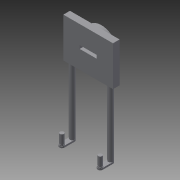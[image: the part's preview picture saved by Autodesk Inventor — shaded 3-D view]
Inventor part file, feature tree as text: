
AUTODESK INVENTOR PART (.ipt)
format: ipt  version: 2015 SP2 (Build 190223200, 223)  size: 163,328 bytes
history: native  units: mm
features: sketch x11, extrude x9
ambient origin geometry x8: Origin, YZ Plane, XZ Plane, XY Plane, X Axis, Y Axis, Z Axis, Center Point
bodies: Solid1 (feature_tree)
feature tree (20):
  sketch  "Sketch1"  dims[d0=5.1mm d1=1.0mm]
  sketch  "Sketch2"  dims[d2=15.0mm d3=12.0mm]
  extrude  "Extrusion1"  Depth=1.0mm
  extrude  "Extrusion2"  Depth=12.0mm
  extrude  "Extrusion4"  Depth=2.0mm TaperAngle=0.0deg
  extrude  "Extrusion5"  Depth=4.0mm TaperAngle=0.0deg
  extrude  "Extrusion6"  Depth=5.1mm
  extrude  "Extrusion7"  Depth=3.0mm TaperAngle=0.0deg
  extrude  "Extrusion8"  Depth=20.0mm TaperAngle=0.0deg
  sketch  "Sketch15"  dims[d25=1.5mm d26=1.5mm]
  extrude  "Extrusion9"  Depth=1.5mm
  extrude  "Extrusion10"  Depth=0.5mm
  sketch  "Sketch20"  dims[d32=1.35mm d33=1.35mm d34=1.35mm d35=1.35mm d36=0.25mm d37=0.0mm]
  sketch  "Sketch3"  dims[d4=10.0mm d5=2.0mm d6=0.0mm]
  sketch  "Sketch7"  dims[d7=2.0mm d8=0.0mm d11=4.0mm d12=0.0mm]
  sketch  "Sketch8"  dims[d13=3.0mm d14=0.0mm d15=5.1mm]
  sketch  "Sketch9"  dims[d16=1.0mm d17=3.0mm d18=0.0mm]
  sketch  "Sketch14"  dims[d19=1.5mm d20=20.0mm d21=0.0mm]
  sketch  "Sketch17"  dims[d27=0.5mm d28=0.0mm d29=1.2mm]
  sketch  "Sketch19"  dims[d30=3.0mm d31=0.0mm]
